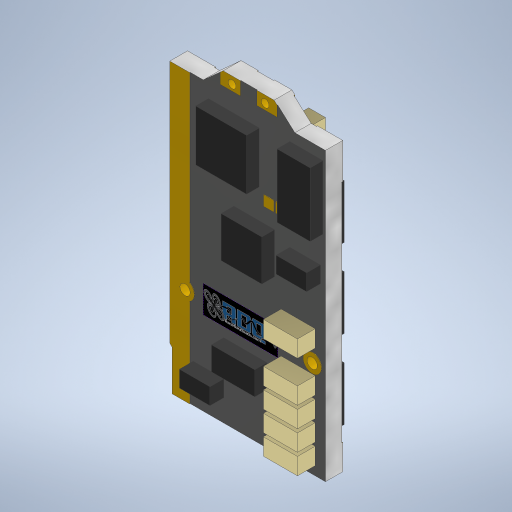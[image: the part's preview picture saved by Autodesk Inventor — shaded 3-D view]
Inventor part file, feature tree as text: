
AUTODESK INVENTOR PART (.ipt)
format: ipt  version: 2023.1 (Build 271208000, 208)  size: 641,024 bytes
history: native  units: in
note: dims shown in document units (in); Inventor stores cm internally (conversion verified against a paired STEP export)
features: extrude x13, sketch x11, chamfer x1, other x1
ambient origin geometry x8: Origin, YZ Plane, XZ Plane, XY Plane, X Axis, Y Axis, Z Axis, Center Point
bodies: Solid1 (feature_tree)
feature tree (26):
  extrude  "Extrusion1"  Depth=1.1811in
  sketch  "Sketch3"  dims[d2=0.063in d3=0.0in d4=1.1102in]
  extrude  "Extrusion2"  Depth=1.1102in
  extrude  "Extrusion3"  Depth=0.3543in
  extrude  "Extrusion4"  Depth=0.0512in
  extrude  "Extrusion5"  Depth=0.0669in
  extrude  "Extrusion6"  Depth=0.0492in
  extrude  "Extrusion7"  Depth=0.374in
  extrude  "Extrusion8"  Depth=0.0394in
  chamfer  "Chamfer1"  Distance=0.2657in
  extrude  "Extrusion9"  Depth=0.1516in
  extrude  "Extrusion10"  Depth=0.0295in
  extrude  "Extrusion11"  Depth=0.128in
  extrude  "Extrusion12"  Depth=0.0276in
  extrude  "Extrusion13"  Depth=0.002in TaperAngle=0.0deg
  sketch  "Sketch12"  dims[d20=0.0079in d21=0.2657in d22=0.1516in d23=0.0295in d24=0.128in d25=0.0276in d26=0.002in d27=0.0in d28=0.0098in d29=0.9449in d30=45.0deg d31=0.002in d32=0.063in d33=0.0in d34=0.0in d35=0.002in d36=0.0in d37=0.0669in d38=0.0in d39=0.0984in d40=0.1378in d41=0.0984in d42=0.1378in d43=0.1339in d44=0.0984in d45=0.1378in d46=0.0984in d47=0.1378in d48=0.0984in d49=0.0787in d50=0.0039in d51=0.0in d52=0.2067in d53=0.2264in d54=0.0394in d55=0.0394in d63=1.1811in d65=0.3051in d66=0.7874in d68=0.2657in d71=0.1339in d72=0.1339in d73=0.25in d74=0.0197in d75=0.0492in d76=0.0in d77=0.1083in d78=0.0039in d79=0.0in d80=0.0039in d81=0.0787in d82=45.0deg d83=0.065in d84=0.1319in d85=0.1969in d86=0.1319in d87=0.065in d88=0.2657in d89=0.0197in d90=0.1319in d91=0.065in d92=0.0197in d93=0.0689in d94=0.0in d95=0.1969in d96=0.1969in d97=0.0531in d98=0.2559in d99=0.1575in d100=0.1575in d101=0.1969in d102=0.3642in d103=0.128in d104=0.2461in d105=0.0394in d106=0.0098in d107=0.0492in d108=0.0in d109=0.1319in d110=0.065in d111=0.0344in d112=0.0394in d113=1.5748in d115=0.0787in d116=0.3937in d118=0.3937in d120=0.1319in d121=0.065in d122=0.0925in d123=0.0689in d124=0.0in d125=0.1181in d126=0.063in d127=0.0197in d128=0.3937in d129=0.0531in d130=0.0in d131=0.1181in d132=0.063in d133=0.1476in d134=0.5118in d135=0.1673in d136=0.0906in d137=0.3937in d138=0.2854in d139=0.0472in d140=0.0in]
  sketch  "Sketch1"  dims[d0=0.5906in d1=1.1811in]
  sketch  "Sketch4"  dims[d5=0.1969in d6=0.3543in]
  sketch  "Sketch5"  dims[d8=0.0787in d9=0.0512in]
  sketch  "Sketch6"  dims[d10=0.2205in d11=0.0669in]
  sketch  "Sketch7"  dims[d12=0.0394in d13=0.0492in]
  sketch  "Sketch8"  dims[d14=0.0709in d15=0.374in]
  sketch  "Sketch9"  dims[d16=0.0394in d17=0.0394in]
  sketch  "Sketch10"  dims[d18=0.0394in]
  sketch  "Sketch11"  dims[d19=0.0394in]
  other  "Image1"
